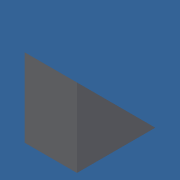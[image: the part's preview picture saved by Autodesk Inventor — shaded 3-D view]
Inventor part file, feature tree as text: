
AUTODESK INVENTOR PART (.ipt)
format: ipt  version: 2018 (Build 220112000, 112)  size: 70,656 bytes
history: native  units: mm
features: extrude x1, sketch x1
ambient origin geometry x8: Origin, YZ Plane, XZ Plane, XY Plane, X Axis, Y Axis, Z Axis, Center Point
bodies: Solid1 (feature_tree)
feature tree (2):
  extrude  "Extrusion1"  Depth=30.0mm
  sketch  "Sketch1"  dims[d0=30.0mm d1=30.0mm d2=20.0mm d3=0.0mm]
